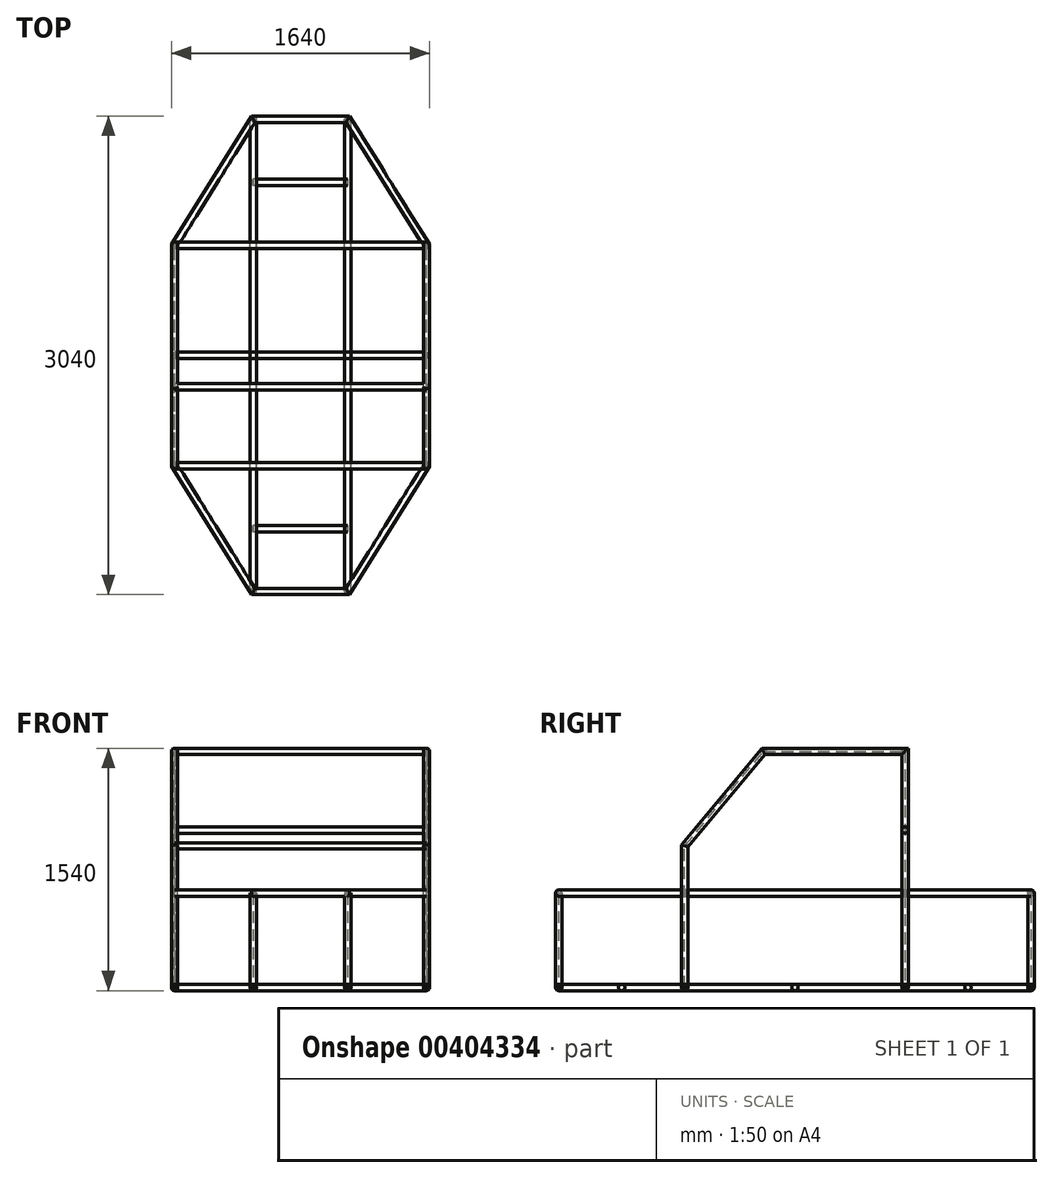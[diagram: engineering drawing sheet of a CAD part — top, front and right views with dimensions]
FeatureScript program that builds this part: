
annotation { "Feature Type Name" : "Feature", "Feature Type Description" : "" }
export const myFeature = defineFeature(function(context is Context, id is Id, definition is map)
    precondition{}
    {
        {
            var Q0;
            Q0=qCreatedBy(makeId("Top.planeOp"),FACE);
            var sketch = newSketch(context, id + "F0", { "sketchPlane" : qUnion([Q0])});
            skLineSegment(sketch, "E0.bottom", {"start": v(-800, -700) * mm, "end": v(800, -700) * mm});
            skLineSegment(sketch, "E0.top", {"start": v(-800, 700) * mm, "end": v(800, 700) * mm});
            skLineSegment(sketch, "E0.left", {"start": v(-800, -700) * mm, "end": v(-800, 700) * mm});
            skLineSegment(sketch, "E0.right", {"start": v(800, -700) * mm, "end": v(800, 700) * mm});
            skPoint(sketch, "E0.middle", {"position": v(0, 0) * mm});
            skLineSegment(sketch, "E1.bottom", {"start": v(-300, -1500) * mm, "end": v(300, -1500) * mm});
            skLineSegment(sketch, "E1.top", {"start": v(-300, 1500) * mm, "end": v(300, 1500) * mm});
            skLineSegment(sketch, "E1.left", {"start": v(-300, -1500) * mm, "end": v(-300, 1500) * mm});
            skLineSegment(sketch, "E1.right", {"start": v(300, -1500) * mm, "end": v(300, 1500) * mm});
            skLineSegment(sketch, "E2", {"start": v(-300, 1100) * mm, "end": v(300, 1100) * mm});
            skLineSegment(sketch, "E3", {"start": v(-300, -1100) * mm, "end": v(300, -1100) * mm});
            skLineSegment(sketch, "E4", {"start": v(-800, 0) * mm, "end": v(800, 0) * mm});
            skCircle(sketch, "E5", {"center": v(-800, -700) * mm, "radius": 20 * mm});
            skCircle(sketch, "E6", {"center": v(-800, 700) * mm, "radius": 20 * mm});
            skCircle(sketch, "E7", {"center": v(800, 700) * mm, "radius": 20 * mm});
            skCircle(sketch, "E8", {"center": v(800, -700) * mm, "radius": 20 * mm});
            skCircle(sketch, "E9", {"center": v(-300, -1500) * mm, "radius": 20 * mm});
            skCircle(sketch, "E10", {"center": v(300, -1500) * mm, "radius": 20 * mm});
            skCircle(sketch, "E11", {"center": v(-300, 1500) * mm, "radius": 20 * mm});
            skCircle(sketch, "E12", {"center": v(300, 1500) * mm, "radius": 20 * mm});
            skLineSegment(sketch, "E13", {"start": v(-800, -700) * mm, "end": v(-300, -1500) * mm, "construction": true});
            skLineSegment(sketch, "E14", {"start": v(300, -1500) * mm, "end": v(800, -700) * mm, "construction": true});
            skLineSegment(sketch, "E15", {"start": v(-800, 700) * mm, "end": v(-300, 1500) * mm, "construction": true});
            skLineSegment(sketch, "E16", {"start": v(300, 1500) * mm, "end": v(800, 700) * mm, "construction": true});
            skSolve(sketch);
        }
        {
            var Q0;
            Q0=qCreatedBy(makeId("Front.planeOp"),FACE);
            var sketch = newSketch(context, id + "F1", { "sketchPlane" : qUnion([Q0])});
            skCircle(sketch, "E17", {"center": v(-800, 0) * mm, "radius": 20 * mm});
            skCircle(sketch, "E18", {"center": v(-300, 0) * mm, "radius": 20 * mm});
            skCircle(sketch, "E19", {"center": v(300, 0) * mm, "radius": 20 * mm});
            skCircle(sketch, "E20", {"center": v(800, 0) * mm, "radius": 20 * mm});
            skSolve(sketch);
        }
        {
            var Q0;
            Q0=qCreatedBy(makeId("Right.planeOp"),FACE);
            var sketch = newSketch(context, id + "F2", { "sketchPlane" : qUnion([Q0])});
            skCircle(sketch, "E21", {"center": v(-1500, 0) * mm, "radius": 20 * mm});
            skCircle(sketch, "E22", {"center": v(-1100, 0) * mm, "radius": 20 * mm});
            skCircle(sketch, "E23", {"center": v(-700, 0) * mm, "radius": 20 * mm});
            skCircle(sketch, "E24", {"center": v(0, 0) * mm, "radius": 20 * mm});
            skCircle(sketch, "E25", {"center": v(700, 0) * mm, "radius": 20 * mm});
            skCircle(sketch, "E26", {"center": v(1100, 0) * mm, "radius": 20 * mm});
            skCircle(sketch, "E27", {"center": v(1500, 0) * mm, "radius": 20 * mm});
            skLineSegment(sketch, "E28", {"start": v(-1500, 0) * mm, "end": v(-1500, 600) * mm, "construction": true});
            skCircle(sketch, "E29", {"center": v(-1500, 600) * mm, "radius": 20 * mm});
            skSolve(sketch);
        }
        {
            var Q0;
            Q0=makeQuery(id+"F1.imprint","IMPRINT",FACE,{"disambiguationData":[TD([[makeQuery(id+"F1.imprint","IMPRINT",EDGE,{"derivedFrom":sQuery(id+"F1.wireOp",EDGE,"E20")}),1.0]])]});
            var Q1;
            Q1=makeQuery(id+"F1.imprint","IMPRINT",FACE,{"disambiguationData":[TD([[makeQuery(id+"F1.imprint","IMPRINT",EDGE,{"derivedFrom":sQuery(id+"F1.wireOp",EDGE,"E17")}),1.0]])]});
            extrude(context, id + "F3", {"entities" : qUnion([Q0, Q1]), "depth" : 1400 * mm, "symmetric" : true});
        }
        {
            var Q0;
            Q0=makeQuery(id+"F1.imprint","IMPRINT",FACE,{"disambiguationData":[TD([[makeQuery(id+"F1.imprint","IMPRINT",EDGE,{"derivedFrom":sQuery(id+"F1.wireOp",EDGE,"E18")}),1.0]])]});
            var Q1;
            Q1=makeQuery(id+"F1.imprint","IMPRINT",FACE,{"disambiguationData":[TD([[makeQuery(id+"F1.imprint","IMPRINT",EDGE,{"derivedFrom":sQuery(id+"F1.wireOp",EDGE,"E19")}),1.0]])]});
            extrude(context, id + "F4", {"entities" : qUnion([Q0, Q1]), "depth" : 3000 * mm, "symmetric" : true});
        }
        {
            var Q0;
            Q0=makeQuery(id+"F2.imprint","IMPRINT",FACE,{"disambiguationData":[TD([[makeQuery(id+"F2.imprint","IMPRINT",EDGE,{"derivedFrom":sQuery(id+"F2.wireOp",EDGE,"E27")}),1.0]])]});
            var Q1;
            Q1=makeQuery(id+"F2.imprint","IMPRINT",FACE,{"disambiguationData":[TD([[makeQuery(id+"F2.imprint","IMPRINT",EDGE,{"derivedFrom":sQuery(id+"F2.wireOp",EDGE,"E21")}),1.0]])]});
            var Q2;
            Q2=makeQuery(id+"F2.imprint","IMPRINT",FACE,{"disambiguationData":[TD([[makeQuery(id+"F2.imprint","IMPRINT",EDGE,{"derivedFrom":sQuery(id+"F2.wireOp",EDGE,"E22")}),1.0]])]});
            var Q3;
            Q3=makeQuery(id+"F2.imprint","IMPRINT",FACE,{"disambiguationData":[TD([[makeQuery(id+"F2.imprint","IMPRINT",EDGE,{"derivedFrom":sQuery(id+"F2.wireOp",EDGE,"E26")}),1.0]])]});
            extrude(context, id + "F5", {"entities" : qUnion([Q0, Q1, Q2, Q3]), "depth" : 600 * mm, "symmetric" : true});
        }
        {
            var Q0;
            Q0=makeQuery(id+"F2.imprint","IMPRINT",FACE,{"disambiguationData":[TD([[makeQuery(id+"F2.imprint","IMPRINT",EDGE,{"derivedFrom":sQuery(id+"F2.wireOp",EDGE,"E23")}),1.0]])]});
            var Q1;
            Q1=makeQuery(id+"F2.imprint","IMPRINT",FACE,{"disambiguationData":[TD([[makeQuery(id+"F2.imprint","IMPRINT",EDGE,{"derivedFrom":sQuery(id+"F2.wireOp",EDGE,"E24")}),1.0]])]});
            var Q2;
            Q2=makeQuery(id+"F2.imprint","IMPRINT",FACE,{"disambiguationData":[TD([[makeQuery(id+"F2.imprint","IMPRINT",EDGE,{"derivedFrom":sQuery(id+"F2.wireOp",EDGE,"E25")}),1.0]])]});
            extrude(context, id + "F6", {"entities" : qUnion([Q0, Q1, Q2]), "depth" : 1600 * mm, "symmetric" : true});
        }
        {
            var Q0;
            Q0=makeQuery(id+"F6.opExtrude","CAP_FACE",FACE,{"disambiguationData":[OSD([sQuery(id+"F2.wireOp",EDGE,"E25")])],"isStart":false});
            var sketch = newSketch(context, id + "F7", { "sketchPlane" : qUnion([Q0])});
            skLineSegment(sketch, "E30.bottom", {"start": v(700, 0) * mm, "end": v(-700, 0) * mm});
            skLineSegment(sketch, "E30.top", {"start": v(700, 1500) * mm, "end": v(-200, 1500) * mm});
            skLineSegment(sketch, "E30.left", {"start": v(700, 0) * mm, "end": v(700, 1500) * mm});
            skLineSegment(sketch, "E30.right", {"start": v(-700, 0) * mm, "end": v(-700, 900) * mm});
            skLineSegment(sketch, "E31", {"start": v(-700, 900) * mm, "end": v(-200, 1500) * mm});
            skSolve(sketch);
        }
        {
            var Q0;
            Q0=makeQuery(id+"F6.opExtrude","CAP_FACE",FACE,{"disambiguationData":[OSD([sQuery(id+"F2.wireOp",EDGE,"E25")])],"isStart":true});
            var sketch = newSketch(context, id + "F8", { "sketchPlane" : qUnion([Q0])});
            skLineSegment(sketch, "E32.bottom", {"start": v(-700, 0) * mm, "end": v(700, 0) * mm});
            skLineSegment(sketch, "E32.top", {"start": v(-700, 1500) * mm, "end": v(200, 1500) * mm});
            skLineSegment(sketch, "E32.left", {"start": v(-700, 0) * mm, "end": v(-700, 1500) * mm});
            skLineSegment(sketch, "E32.right", {"start": v(700, 0) * mm, "end": v(700, 900) * mm});
            skLineSegment(sketch, "E33", {"start": v(700, 900) * mm, "end": v(200, 1500) * mm});
            skCircle(sketch, "E34", {"center": v(700, 900) * mm, "radius": 20 * mm});
            skCircle(sketch, "E35", {"center": v(200, 1500) * mm, "radius": 20 * mm});
            skCircle(sketch, "E36", {"center": v(-700, 1500) * mm, "radius": 20 * mm});
            skCircle(sketch, "E37", {"center": v(-700, 1000) * mm, "radius": 20 * mm});
            skSolve(sketch);
        }
        {
            var Q0;
            {var subQ0=sQuery(id+"F8.wireOp",EDGE,"E33");var subQ1=sQuery(id+"F8.wireOp",EDGE,"E32.right");var subQ2=makeQuery(id+"F8.imprint","INTERSECT",VERTEX,{"derivedFrom":[subQ1,subQ0]});Q0=makeQuery(id+"F8.imprint","IMPRINT",FACE,{"disambiguationData":[TD([[makeQuery(id+"F8.imprint","IMPRINT",EDGE,{"disambiguationData":[TD([[subQ2,1.0]])],"derivedFrom":subQ1}),-1.0]])]});}
            var Q1;
            {var subQ0=sQuery(id+"F8.wireOp",EDGE,"E33");var subQ1=sQuery(id+"F8.wireOp",EDGE,"E32.right");var subQ2=makeQuery(id+"F8.imprint","INTERSECT",VERTEX,{"derivedFrom":[subQ1,subQ0]});Q1=makeQuery(id+"F8.imprint","IMPRINT",FACE,{"disambiguationData":[TD([[makeQuery(id+"F8.imprint","IMPRINT",EDGE,{"disambiguationData":[TD([[subQ2,1.0]])],"derivedFrom":subQ1}),1.0]])]});}
            var Q2;
            {var subQ0=sQuery(id+"F8.wireOp",EDGE,"E33");var subQ1=sQuery(id+"F8.wireOp",EDGE,"E32.top");var subQ2=makeQuery(id+"F8.imprint","INTERSECT",VERTEX,{"derivedFrom":[subQ1,subQ0]});Q2=makeQuery(id+"F8.imprint","IMPRINT",FACE,{"disambiguationData":[TD([[makeQuery(id+"F8.imprint","IMPRINT",EDGE,{"disambiguationData":[TD([[subQ2,1.0]])],"derivedFrom":subQ1}),1.0]])]});}
            var Q3;
            {var subQ0=sQuery(id+"F8.wireOp",EDGE,"E33");var subQ1=sQuery(id+"F8.wireOp",EDGE,"E32.top");var subQ2=makeQuery(id+"F8.imprint","INTERSECT",VERTEX,{"derivedFrom":[subQ1,subQ0]});Q3=makeQuery(id+"F8.imprint","IMPRINT",FACE,{"disambiguationData":[TD([[makeQuery(id+"F8.imprint","IMPRINT",EDGE,{"disambiguationData":[TD([[subQ2,1.0]])],"derivedFrom":subQ1}),-1.0]])]});}
            var Q4;
            {var subQ0=sQuery(id+"F8.wireOp",EDGE,"E32.left");var subQ1=sQuery(id+"F8.wireOp",EDGE,"E32.top");var subQ2=makeQuery(id+"F8.imprint","INTERSECT",VERTEX,{"derivedFrom":[subQ1,subQ0]});Q4=makeQuery(id+"F8.imprint","IMPRINT",FACE,{"disambiguationData":[TD([[makeQuery(id+"F8.imprint","IMPRINT",EDGE,{"disambiguationData":[TD([[subQ2,-1.0]])],"derivedFrom":subQ1}),-1.0]])]});}
            var Q5;
            {var subQ0=sQuery(id+"F8.wireOp",EDGE,"E32.left");var subQ1=sQuery(id+"F8.wireOp",EDGE,"E32.top");var subQ2=makeQuery(id+"F8.imprint","INTERSECT",VERTEX,{"derivedFrom":[subQ1,subQ0]});Q5=makeQuery(id+"F8.imprint","IMPRINT",FACE,{"disambiguationData":[TD([[makeQuery(id+"F8.imprint","IMPRINT",EDGE,{"disambiguationData":[TD([[subQ2,-1.0]])],"derivedFrom":subQ1}),1.0]])]});}
            var Q6;
            {var subQ0=sQuery(id+"F8.wireOp",EDGE,"E37");var subQ1=sQuery(id+"F8.wireOp",EDGE,"E32.left");var subQ2=makeQuery(id+"F8.imprint","INTERSECT",VERTEX,{"disambiguationData":[OD(0.0)],"derivedFrom":[subQ1,subQ0]});Q6=makeQuery(id+"F8.imprint","IMPRINT",FACE,{"disambiguationData":[TD([[makeQuery(id+"F8.imprint","IMPRINT",EDGE,{"disambiguationData":[TD([[subQ2,-1.0]])],"derivedFrom":subQ1}),1.0]])]});}
            var Q7;
            {var subQ0=sQuery(id+"F8.wireOp",EDGE,"E37");var subQ1=sQuery(id+"F8.wireOp",EDGE,"E32.left");var subQ2=makeQuery(id+"F8.imprint","INTERSECT",VERTEX,{"disambiguationData":[OD(0.0)],"derivedFrom":[subQ1,subQ0]});Q7=makeQuery(id+"F8.imprint","IMPRINT",FACE,{"disambiguationData":[TD([[makeQuery(id+"F8.imprint","IMPRINT",EDGE,{"disambiguationData":[TD([[subQ2,-1.0]])],"derivedFrom":subQ1}),-1.0]])]});}
            extrude(context, id + "F9", {"entities" : qUnion([Q0, Q1, Q2, Q3, Q4, Q5, Q6, Q7]), "oppositeDirection" : true, "depth" : 1600 * mm});
        }
        {
            var Q0;
            {var subQ0=sQuery(id+"F0.wireOp",EDGE,"E1.left");var subQ1=sQuery(id+"F0.wireOp",EDGE,"E1.bottom");var subQ2=makeQuery(id+"F0.imprint","INTERSECT",VERTEX,{"derivedFrom":[subQ1,subQ0]});Q0=makeQuery(id+"F0.imprint","IMPRINT",FACE,{"disambiguationData":[TD([[makeQuery(id+"F0.imprint","IMPRINT",EDGE,{"disambiguationData":[TD([[subQ2,-1.0]])],"derivedFrom":subQ1}),-1.0]])]});}
            var Q1;
            {var subQ0=sQuery(id+"F0.wireOp",EDGE,"E1.right");var subQ1=sQuery(id+"F0.wireOp",EDGE,"E1.bottom");var subQ2=makeQuery(id+"F0.imprint","INTERSECT",VERTEX,{"derivedFrom":[subQ1,subQ0]});Q1=makeQuery(id+"F0.imprint","IMPRINT",FACE,{"disambiguationData":[TD([[makeQuery(id+"F0.imprint","IMPRINT",EDGE,{"disambiguationData":[TD([[subQ2,1.0]])],"derivedFrom":subQ1}),-1.0]])]});}
            var Q2;
            {var subQ0=sQuery(id+"F0.wireOp",EDGE,"E1.right");var subQ1=sQuery(id+"F0.wireOp",EDGE,"E1.top");var subQ2=makeQuery(id+"F0.imprint","INTERSECT",VERTEX,{"derivedFrom":[subQ1,subQ0]});Q2=makeQuery(id+"F0.imprint","IMPRINT",FACE,{"disambiguationData":[TD([[makeQuery(id+"F0.imprint","IMPRINT",EDGE,{"disambiguationData":[TD([[subQ2,1.0]])],"derivedFrom":subQ1}),1.0]])]});}
            var Q3;
            {var subQ0=sQuery(id+"F0.wireOp",EDGE,"E1.left");var subQ1=sQuery(id+"F0.wireOp",EDGE,"E1.top");var subQ2=makeQuery(id+"F0.imprint","INTERSECT",VERTEX,{"derivedFrom":[subQ1,subQ0]});Q3=makeQuery(id+"F0.imprint","IMPRINT",FACE,{"disambiguationData":[TD([[makeQuery(id+"F0.imprint","IMPRINT",EDGE,{"disambiguationData":[TD([[subQ2,-1.0]])],"derivedFrom":subQ1}),1.0]])]});}
            extrude(context, id + "F10", {"entities" : qUnion([Q0, Q1, Q2, Q3]), "depth" : 600 * mm});
        }
        {
            var Q0;
            {var subQ0=sQuery(id+"F0.wireOp",EDGE,"E0.right");var subQ1=sQuery(id+"F0.wireOp",EDGE,"E0.bottom");var subQ2=makeQuery(id+"F0.imprint","INTERSECT",VERTEX,{"derivedFrom":[subQ1,subQ0]});Q0=makeQuery(id+"F0.imprint","IMPRINT",FACE,{"disambiguationData":[TD([[makeQuery(id+"F0.imprint","IMPRINT",EDGE,{"disambiguationData":[TD([[subQ2,1.0]])],"derivedFrom":subQ1}),-1.0]])]});}
            var Q1;
            Q1=sQuery(id+"F7.wireOp",EDGE,"E30.right");
            var Q2;
            Q2=sQuery(id+"F7.wireOp",EDGE,"E31");
            var Q3;
            Q3=sQuery(id+"F7.wireOp",EDGE,"E30.top");
            var Q4;
            Q4=sQuery(id+"F7.wireOp",EDGE,"E30.left");
            sweep(context, id + "F11", {"profiles" : qUnion([Q0]), "path" : qUnion([Q1, Q2, Q3, Q4])});
        }
        {
            var Q0;
            {var subQ0=sQuery(id+"F0.wireOp",EDGE,"E0.left");var subQ1=sQuery(id+"F0.wireOp",EDGE,"E0.bottom");var subQ2=makeQuery(id+"F0.imprint","INTERSECT",VERTEX,{"derivedFrom":[subQ1,subQ0]});Q0=makeQuery(id+"F0.imprint","IMPRINT",FACE,{"disambiguationData":[TD([[makeQuery(id+"F0.imprint","IMPRINT",EDGE,{"disambiguationData":[TD([[subQ2,-1.0]])],"derivedFrom":subQ1}),-1.0]])]});}
            var Q1;
            Q1=sQuery(id+"F8.wireOp",EDGE,"E32.top");
            var Q2;
            Q2=sQuery(id+"F8.wireOp",EDGE,"E32.left");
            var Q3;
            Q3=sQuery(id+"F8.wireOp",EDGE,"E33");
            var Q4;
            Q4=sQuery(id+"F8.wireOp",EDGE,"E32.right");
            sweep(context, id + "F12", {"profiles" : qUnion([Q0]), "path" : qUnion([Q1, Q2, Q3, Q4])});
        }
        {
            var Q0;
            Q0=makeQuery(id+"F10.opExtrude","CAP_FACE",FACE,{"disambiguationData":[OSD([sQuery(id+"F0.wireOp",EDGE,"E1.top"),sQuery(id+"F0.wireOp",EDGE,"E1.right"),sQuery(id+"F0.wireOp",EDGE,"E12")])],"isStart":false});
            var sketch = newSketch(context, id + "F13", { "sketchPlane" : qUnion([Q0])});
            skLineSegment(sketch, "E38", {"start": v(-300, 1500) * mm, "end": v(-800, 700) * mm});
            skLineSegment(sketch, "E39", {"start": v(300, 1500) * mm, "end": v(-300, 1500) * mm});
            skLineSegment(sketch, "E40", {"start": v(300, 1500) * mm, "end": v(800, 700) * mm});
            skLineSegment(sketch, "E41", {"start": v(800, 700) * mm, "end": v(800, -700) * mm});
            skLineSegment(sketch, "E42", {"start": v(800, -700) * mm, "end": v(300, -1500) * mm});
            skLineSegment(sketch, "E43", {"start": v(300, -1500) * mm, "end": v(-300, -1500) * mm});
            skLineSegment(sketch, "E44", {"start": v(-300, -1500) * mm, "end": v(-800, -700) * mm});
            skLineSegment(sketch, "E45", {"start": v(-800, -700) * mm, "end": v(-800, 700) * mm});
            skPoint(sketch, "E46.end.orphan", {"position": v(0, -700) * mm});
            skPoint(sketch, "E46.start.orphan", {"position": v(0, -1500) * mm});
            skLineSegment(sketch, "E47", {"start": v(-800, -700) * mm, "end": v(800, -700) * mm, "construction": true});
            skLineSegment(sketch, "E48", {"start": v(-300, -1500) * mm, "end": v(-300, -700) * mm, "construction": true});
            skLineSegment(sketch, "E49", {"start": v(300, -1500) * mm, "end": v(300, -700) * mm, "construction": true});
            skSolve(sketch);
        }
        {
            var Q0;
            Q0=makeQuery(id+"F2.imprint","IMPRINT",FACE,{"disambiguationData":[TD([[makeQuery(id+"F2.imprint","IMPRINT",EDGE,{"derivedFrom":sQuery(id+"F2.wireOp",EDGE,"E29")}),1.0]])]});
            var Q1;
            Q1=sQuery(id+"F13.wireOp",EDGE,"E43");
            var Q2;
            Q2=sQuery(id+"F13.wireOp",EDGE,"E44");
            var Q3;
            Q3=sQuery(id+"F13.wireOp",EDGE,"E45");
            var Q4;
            Q4=sQuery(id+"F13.wireOp",EDGE,"E38");
            var Q5;
            Q5=sQuery(id+"F13.wireOp",EDGE,"E39");
            var Q6;
            Q6=sQuery(id+"F13.wireOp",EDGE,"E40");
            var Q7;
            Q7=sQuery(id+"F13.wireOp",EDGE,"E41");
            var Q8;
            Q8=sQuery(id+"F13.wireOp",EDGE,"E42");
            sweep(context, id + "F14", {"profiles" : qUnion([Q0]), "path" : qUnion([Q1, Q2, Q3, Q4, Q5, Q6, Q7, Q8])});
        }
    });
